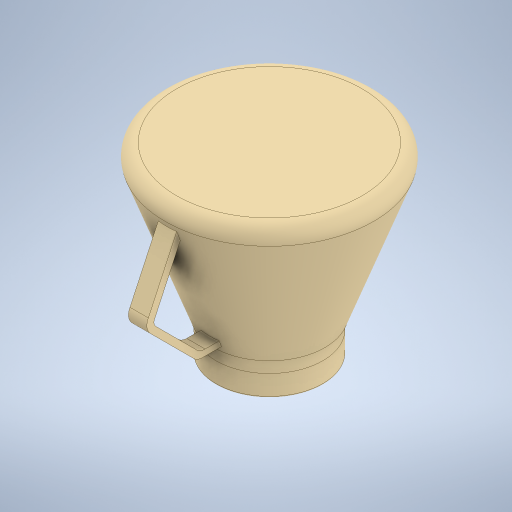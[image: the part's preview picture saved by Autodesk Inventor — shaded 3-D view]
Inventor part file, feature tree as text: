
AUTODESK INVENTOR PART (.ipt)
format: ipt  version: 2024 (Build 280153000, 153)  size: 355,840 bytes
history: native  units: mm
features: fillet x3, sketch x3, extrude x2, other x1, plane x1, revolve x1, shell x1
ambient origin geometry x8: Origin, YZ Plane, XZ Plane, XY Plane, X Axis, Y Axis, Z Axis, Center Point
bodies: Body1 (feature_tree)
feature tree (12):
  extrude  "Extrusion2"  Depth=255.0mm TaperAngle=0.0deg
  other  "Flächenverjüngung1"
  fillet  "Rundung1"  Radius=3.490659mm
  plane  "Arbeitsebene5"
  revolve  "Umdrehung1"
  fillet  "Rundung2"  Radius=20.0mm
  shell  "Wandung1"  Thickness=0.0mm
  extrude  "Extrusion4"  TaperAngle=90.0deg  [1 undecoded]
  fillet  "Rundung3"  Radius=60.0mm
  sketch  "Skizze5"  dims[d8=360.0mm d9=255.0mm d10=0.0mm d11=3.490659mm d13=20.0mm d14=0.0mm]
  sketch  "Skizze7"  dims[d15=45.0mm d16=90.0deg d17=60.0mm]
  sketch  "Skizze8"  dims[d18=8.0mm d22=70.0mm d23=20.0mm d24=100.0mm d25=20.0mm d26=19.198622mm d27=100.0mm d28=135.0deg d29=30.0mm d33=5.0mm d35=5.0mm d36=5.0mm d37=20.0mm d38=10.0mm d39=94.0mm d40=20.0mm d41=6.974064mm d42=30.0mm d43=0.0mm d44=1.0mm d45=30.0mm d46=2.0mm]
note: 1 required parameter value undecoded (feature->parameter linkage not recoverable at this tier; creation-order binding heuristic only, values carry confidence <= 0.55)
